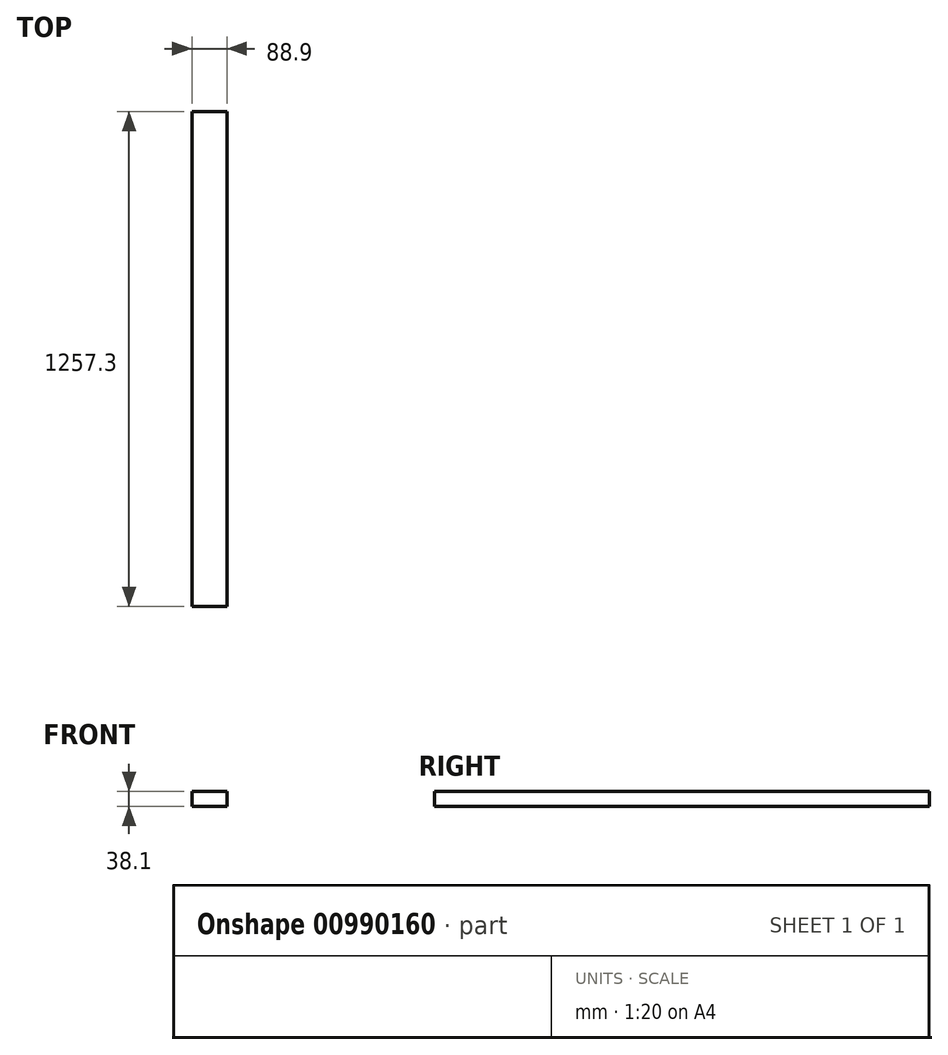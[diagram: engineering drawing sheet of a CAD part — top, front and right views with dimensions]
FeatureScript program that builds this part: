
annotation { "Feature Type Name" : "Feature", "Feature Type Description" : "" }
export const myFeature = defineFeature(function(context is Context, id is Id, definition is map)
    precondition{}
    {
        {
            assignVariable(context, id + "F0", {"name" : "w", "anyValue" : 38.1 * mm});
        }
        {
            var Q0;
            Q0=qCreatedBy(makeId("Top.planeOp"),FACE);
            var sketch = newSketch(context, id + "F1", { "sketchPlane" : qUnion([Q0])});
            skLineSegment(sketch, "E0.bottom", {"start": v(44.45, 628.65) * mm, "end": v(-44.45, 628.65) * mm});
            skLineSegment(sketch, "E0.top", {"start": v(44.45, -628.65) * mm, "end": v(-44.45, -628.65) * mm});
            skLineSegment(sketch, "E0.left", {"start": v(44.45, 628.65) * mm, "end": v(44.45, -628.65) * mm});
            skLineSegment(sketch, "E0.right", {"start": v(-44.45, 628.65) * mm, "end": v(-44.45, -628.65) * mm});
            skPoint(sketch, "E0.middle", {"position": v(0, 0) * mm});
            skSolve(sketch);
        }
        {
            var Q0;
            Q0=qSketchRegion(id+"F1",true);
            extrude(context, id + "F2", {"entities" : qUnion([Q0]), "depth" : getVariable(context, 'w'), "offsetDistance" : 25.4 * mm});
        }
    });
